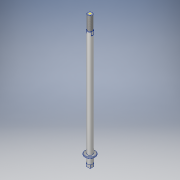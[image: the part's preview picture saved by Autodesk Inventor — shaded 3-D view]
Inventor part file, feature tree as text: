
AUTODESK INVENTOR PART (.ipt)
format: ipt  version: 2019 (Build 230136000, 136)  size: 167,936 bytes
history: native  units: mm
features: sketch x7, extrude x6, fillet x3, thread x1
ambient origin geometry x8: Origin, YZ Plane, XZ Plane, XY Plane, X Axis, Y Axis, Z Axis, Center Point
bodies: Solid1 (feature_tree)
feature tree (17):
  extrude  "Extrusion1"  Depth=0.5mm TaperAngle=0.0deg
  fillet  "Fillet1"  Radius=0.5mm
  extrude  "Extrusion2"  Depth=10.0mm TaperAngle=0.0deg
  extrude  "Extrusion3"  Depth=8.0mm
  extrude  "Extrusion4"  Depth=3.5mm
  extrude  "Extrusion5"  Depth=3.5mm TaperAngle=0.0deg
  extrude  "Extrusion6"  Depth=0.5mm
  fillet  "Fillet2"  Radius=0.5mm
  fillet  "Fillet3"  Radius=10.0mm
  thread  "Thread1"  [1 undecoded]
  sketch  "Sketch7"
  sketch  "Sketch1"  dims[d0=15.0mm d1=2.0mm d2=0.0mm d3=0.5mm]
  sketch  "Sketch2"  dims[d4=8.0mm d5=10.0mm d6=0.0mm]
  sketch  "Sketch3"  dims[d7=5.0mm d8=0.0mm d9=8.0mm]
  sketch  "Sketch4"  dims[d10=157.0mm d11=0.0mm d12=3.5mm]
  sketch  "Sketch5"  dims[d13=3.5mm d14=5.0mm d15=0.0mm]
  sketch  "Sketch6"  dims[d16=21.0mm d17=0.0mm d18=0.5mm d19=0.5mm d20=10.0mm d21=0.0mm]
note: 1 required parameter value undecoded (feature->parameter linkage not recoverable at this tier; creation-order binding heuristic only, values carry confidence <= 0.55)
